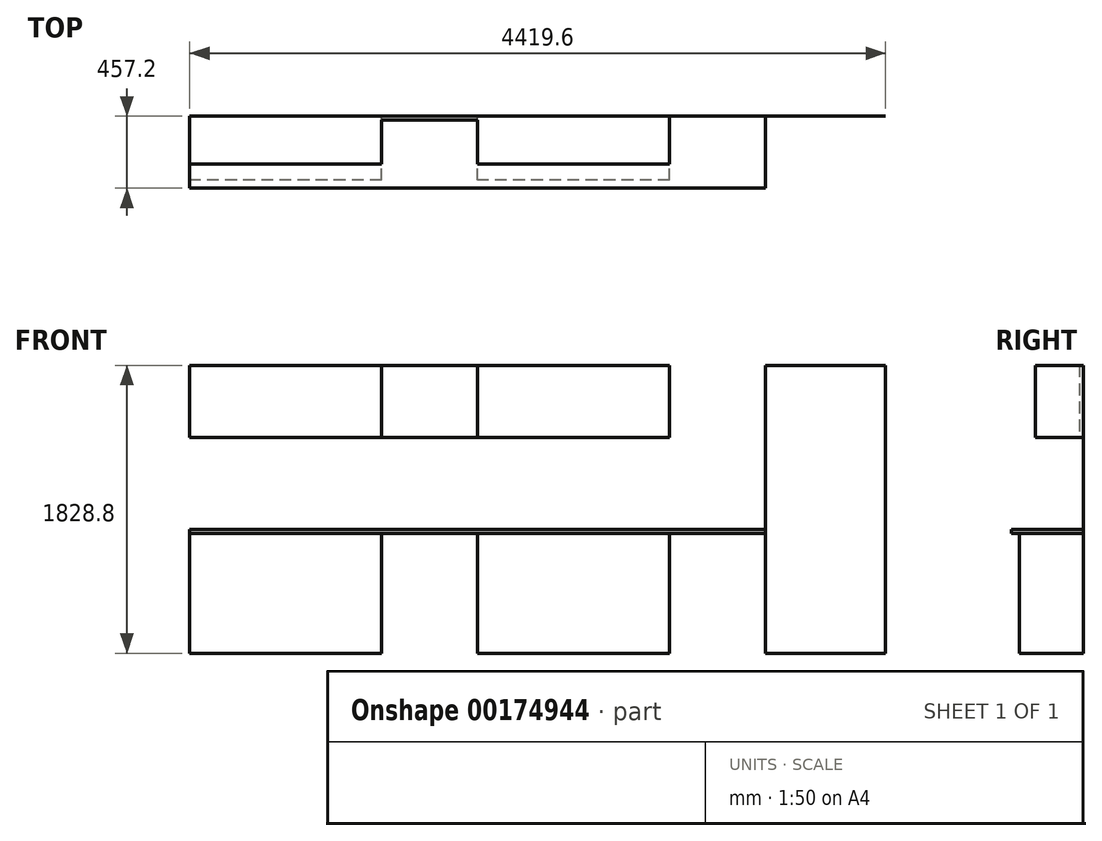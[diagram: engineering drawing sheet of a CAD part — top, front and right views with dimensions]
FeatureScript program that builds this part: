
annotation { "Feature Type Name" : "Feature", "Feature Type Description" : "" }
export const myFeature = defineFeature(function(context is Context, id is Id, definition is map)
    precondition{}
    {
        {
            var Q0;
            Q0=qCreatedBy(makeId("Front.planeOp"),FACE);
            var sketch = newSketch(context, id + "F0", { "sketchPlane" : qUnion([Q0])});
            skLineSegment(sketch, "E0.bottom", {"start": v(914.4, -381) * mm, "end": v(-914.4, -381) * mm});
            skLineSegment(sketch, "E0.top", {"start": v(914.4, 381) * mm, "end": v(-914.4, 381) * mm});
            skLineSegment(sketch, "E0.left", {"start": v(914.4, -381) * mm, "end": v(914.4, 381) * mm});
            skLineSegment(sketch, "E0.right", {"start": v(-914.4, -381) * mm, "end": v(-914.4, 381) * mm});
            skPoint(sketch, "E0.middle", {"position": v(0, 0) * mm});
            skLineSegment(sketch, "E1", {"start": v(-914.4, -584.2) * mm, "end": v(914.4, -584.2) * mm});
            skLineSegment(sketch, "E2", {"start": v(304.8, 381) * mm, "end": v(304.8, -381) * mm});
            skLineSegment(sketch, "E3", {"start": v(-304.8, 381) * mm, "end": v(-304.8, -381) * mm});
            skLineSegment(sketch, "E4.bottom", {"start": v(914.4, -381) * mm, "end": v(1524, -381) * mm});
            skLineSegment(sketch, "E4.top", {"start": v(914.4, 381) * mm, "end": v(1524, 381) * mm});
            skLineSegment(sketch, "E4.right", {"start": v(1524, -381) * mm, "end": v(1524, 381) * mm});
            skLineSegment(sketch, "E5.bottom", {"start": v(1524, -381) * mm, "end": v(2286, -381) * mm});
            skLineSegment(sketch, "E5.top", {"start": v(1524, 1447.8) * mm, "end": v(2286, 1447.8) * mm});
            skLineSegment(sketch, "E5.left", {"start": v(1524, -381) * mm, "end": v(1524, 1447.8) * mm});
            skLineSegment(sketch, "E5.right", {"start": v(2286, -381) * mm, "end": v(2286, 1447.8) * mm});
            skLineSegment(sketch, "E6.bottom", {"start": v(-914.4, -381) * mm, "end": v(-1524, -381) * mm});
            skLineSegment(sketch, "E6.right", {"start": v(-1524, -381) * mm, "end": v(-1524, 381) * mm});
            skLineSegment(sketch, "E7.bottom", {"start": v(-1524, -381) * mm, "end": v(-2133.6, -381) * mm});
            skLineSegment(sketch, "E7.top", {"start": v(-1524, 381) * mm, "end": v(-2133.6, 381) * mm});
            skLineSegment(sketch, "E7.right", {"start": v(-2133.6, -381) * mm, "end": v(-2133.6, 381) * mm});
            skLineSegment(sketch, "E8.bottom", {"start": v(-914.4, 1447.8) * mm, "end": v(-304.8, 1447.8) * mm});
            skLineSegment(sketch, "E8.top", {"start": v(-914.4, 990.6) * mm, "end": v(-304.8, 990.6) * mm});
            skLineSegment(sketch, "E8.right", {"start": v(1524, 1447.8) * mm, "end": v(1524, 990.6) * mm});
            skLineSegment(sketch, "E9", {"start": v(-914.4, 1447.8) * mm, "end": v(-914.4, 990.6) * mm});
            skLineSegment(sketch, "E10", {"start": v(-1524, 381) * mm, "end": v(-914.4, 381) * mm});
            skLineSegment(sketch, "E11.bottom", {"start": v(-914.4, 990.6) * mm, "end": v(-1524, 990.6) * mm});
            skLineSegment(sketch, "E11.top", {"start": v(-914.4, 1447.8) * mm, "end": v(-1524, 1447.8) * mm});
            skLineSegment(sketch, "E11.left", {"start": v(-914.4, 990.6) * mm, "end": v(-914.4, 1447.8) * mm});
            skLineSegment(sketch, "E11.right", {"start": v(-1524, 990.6) * mm, "end": v(-1524, 1447.8) * mm});
            skLineSegment(sketch, "E12.bottom", {"start": v(-1524, 1447.8) * mm, "end": v(-2133.6, 1447.8) * mm});
            skLineSegment(sketch, "E12.top", {"start": v(-1524, 990.6) * mm, "end": v(-2133.6, 990.6) * mm});
            skLineSegment(sketch, "E12.left", {"start": v(-1524, 1447.8) * mm, "end": v(-1524, 990.6) * mm});
            skLineSegment(sketch, "E12.right", {"start": v(-2133.6, 1447.8) * mm, "end": v(-2133.6, 990.6) * mm});
            skLineSegment(sketch, "E13", {"start": v(-304.8, 1447.8) * mm, "end": v(-304.8, 990.6) * mm});
            skLineSegment(sketch, "E14", {"start": v(304.8, 1447.8) * mm, "end": v(304.8, 990.6) * mm});
            skLineSegment(sketch, "E15.trimOffspring", {"start": v(304.8, 1447.8) * mm, "end": v(1524, 1447.8) * mm});
            skLineSegment(sketch, "E16.trimOffspring", {"start": v(304.8, 990.6) * mm, "end": v(1524, 990.6) * mm});
            skLineSegment(sketch, "E17", {"start": v(-304.8, 1447.8) * mm, "end": v(304.8, 1447.8) * mm});
            skLineSegment(sketch, "E18", {"start": v(-304.8, 990.6) * mm, "end": v(304.8, 990.6) * mm});
            skLineSegment(sketch, "E19", {"start": v(914.4, 1447.8) * mm, "end": v(914.4, 990.6) * mm});
            skSolve(sketch);
        }
        {
            var Q0;
            {var subQ2=sQuery(id+"F0.wireOp",EDGE,"E2");Q0=makeQuery(id+"F0.imprint","IMPRINT",FACE,{"disambiguationData":[TD([[makeQuery(id+"F0.imprint","IMPRINT",EDGE,{"derivedFrom":subQ2}),1.0]])]});}
            var Q1;
            Q1=makeQuery(id+"F0.imprint","IMPRINT",FACE,{"disambiguationData":[TD([[makeQuery(id+"F0.imprint","IMPRINT",EDGE,{"derivedFrom":sQuery(id+"F0.wireOp",EDGE,"E7.bottom")}),-1.0]])]});
            var Q2;
            Q2=makeQuery(id+"F0.imprint","IMPRINT",FACE,{"disambiguationData":[TD([[makeQuery(id+"F0.imprint","IMPRINT",EDGE,{"derivedFrom":sQuery(id+"F0.wireOp",EDGE,"E6.bottom")}),-1.0]])]});
            var Q3;
            {var subQ0=sQuery(id+"F0.wireOp",EDGE,"E2");Q3=makeQuery(id+"F0.imprint","IMPRINT",FACE,{"disambiguationData":[TD([[makeQuery(id+"F0.imprint","IMPRINT",EDGE,{"derivedFrom":subQ0}),-1.0]])]});}
            extrude(context, id + "F1", {"entities" : qUnion([Q0, Q1, Q2, Q3]), "depth" : 406.4 * mm, "offsetDistance" : 25.4 * mm});
        }
        {
            var Q0;
            {var subQ3=sQuery(id+"F0.wireOp",EDGE,"E5.bottom");Q0=makeQuery(id+"F0.imprint","IMPRINT",FACE,{"disambiguationData":[TD([[makeQuery(id+"F0.imprint","IMPRINT",EDGE,{"derivedFrom":subQ3}),1.0]])]});}
            extrude(context, id + "F2", {"entities" : qUnion([Q0]), "operationType" : NewBodyOperationType.ADD, "depth" : 0.25 * mm, "offsetDistance" : 25.4 * mm});
        }
        {
            var Q0;
            Q0=makeQuery(id+"F0.imprint","IMPRINT",FACE,{"disambiguationData":[TD([[makeQuery(id+"F0.imprint","IMPRINT",EDGE,{"derivedFrom":sQuery(id+"F0.wireOp",EDGE,"E11.bottom")}),-1.0]])]});
            var Q1;
            Q1=makeQuery(id+"F0.imprint","IMPRINT",FACE,{"disambiguationData":[TD([[makeQuery(id+"F0.imprint","IMPRINT",EDGE,{"derivedFrom":sQuery(id+"F0.wireOp",EDGE,"E12.bottom")}),1.0]])]});
            var Q2;
            {var subQ0=sQuery(id+"F0.wireOp",EDGE,"E14");Q2=makeQuery(id+"F0.imprint","IMPRINT",FACE,{"disambiguationData":[TD([[makeQuery(id+"F0.imprint","IMPRINT",EDGE,{"derivedFrom":subQ0}),1.0]])]});}
            var Q3;
            Q3=makeQuery(id+"F0.imprint","IMPRINT",FACE,{"disambiguationData":[TD([[makeQuery(id+"F0.imprint","IMPRINT",EDGE,{"derivedFrom":sQuery(id+"F0.wireOp",EDGE,"E13")}),1.0]])]});
            extrude(context, id + "F3", {"entities" : qUnion([Q0, Q1, Q2, Q3]), "operationType" : NewBodyOperationType.ADD, "depth" : 304.8 * mm, "offsetDistance" : 25.4 * mm});
        }
        {
            var Q0;
            Q0=makeQuery(id+"F1.opExtrude","SWEPT_FACE",FACE,{"disambiguationData":[OSD([sQuery(id+"F0.wireOp",EDGE,"E7.top"),sQuery(id+"F0.wireOp",EDGE,"E10")])]});
            var sketch = newSketch(context, id + "F4", { "sketchPlane" : qUnion([Q0])});
            skLineSegment(sketch, "E20.bottom", {"start": v(1523.58, 0) * mm, "end": v(-2133.6, 0) * mm});
            skLineSegment(sketch, "E20.top", {"start": v(1523.58, -457.2) * mm, "end": v(-2133.6, -457.2) * mm});
            skLineSegment(sketch, "E20.left", {"start": v(1523.58, 0) * mm, "end": v(1523.58, -457.2) * mm});
            skLineSegment(sketch, "E20.right", {"start": v(-2133.6, 0) * mm, "end": v(-2133.6, -457.2) * mm});
            skSolve(sketch);
        }
        {
            var Q0;
            {var subQ1=sQuery(id+"F0.wireOp",EDGE,"E10");var subQ5=makeQuery(id+"F1.opExtrude","CAP_EDGE",EDGE,{"disambiguationData":[OSD([sQuery(id+"F0.wireOp",EDGE,"E7.top"),subQ1])],"isStart":false});Q0=makeQuery(id+"F4.imprint","IMPRINT",FACE,{"disambiguationData":[TD([[makeQuery(id+"F4.imprint","IMPRINT",EDGE,{"derivedFrom":subQ5}),-1.0]])]});}
            var Q1;
            {var subQ1=sQuery(id+"F4.wireOp",EDGE,"E20.top");Q1=makeQuery(id+"F4.imprint","IMPRINT",FACE,{"disambiguationData":[TD([[makeQuery(id+"F4.imprint","IMPRINT",EDGE,{"derivedFrom":subQ1}),-1.0]])]});}
            extrude(context, id + "F5", {"entities" : qUnion([Q0, Q1]), "depth" : 25.4 * mm, "offsetDistance" : 25.4 * mm});
        }
        {
            var Q0;
            Q0=makeQuery(id+"F0.imprint","IMPRINT",FACE,{"disambiguationData":[TD([[makeQuery(id+"F0.imprint","IMPRINT",EDGE,{"derivedFrom":sQuery(id+"F0.wireOp",EDGE,"E13")}),1.0]])]});
            var Q1;
            Q1=makeQuery(id+"F0.imprint","IMPRINT",FACE,{"disambiguationData":[TD([[makeQuery(id+"F0.imprint","IMPRINT",EDGE,{"derivedFrom":sQuery(id+"F0.wireOp",EDGE,"E8.bottom")}),-1.0]])]});
            extrude(context, id + "F6", {"entities" : qUnion([Q0, Q1]), "operationType" : NewBodyOperationType.ADD, "depth" : 25.4 * mm, "offsetDistance" : 25.4 * mm});
        }
    });
